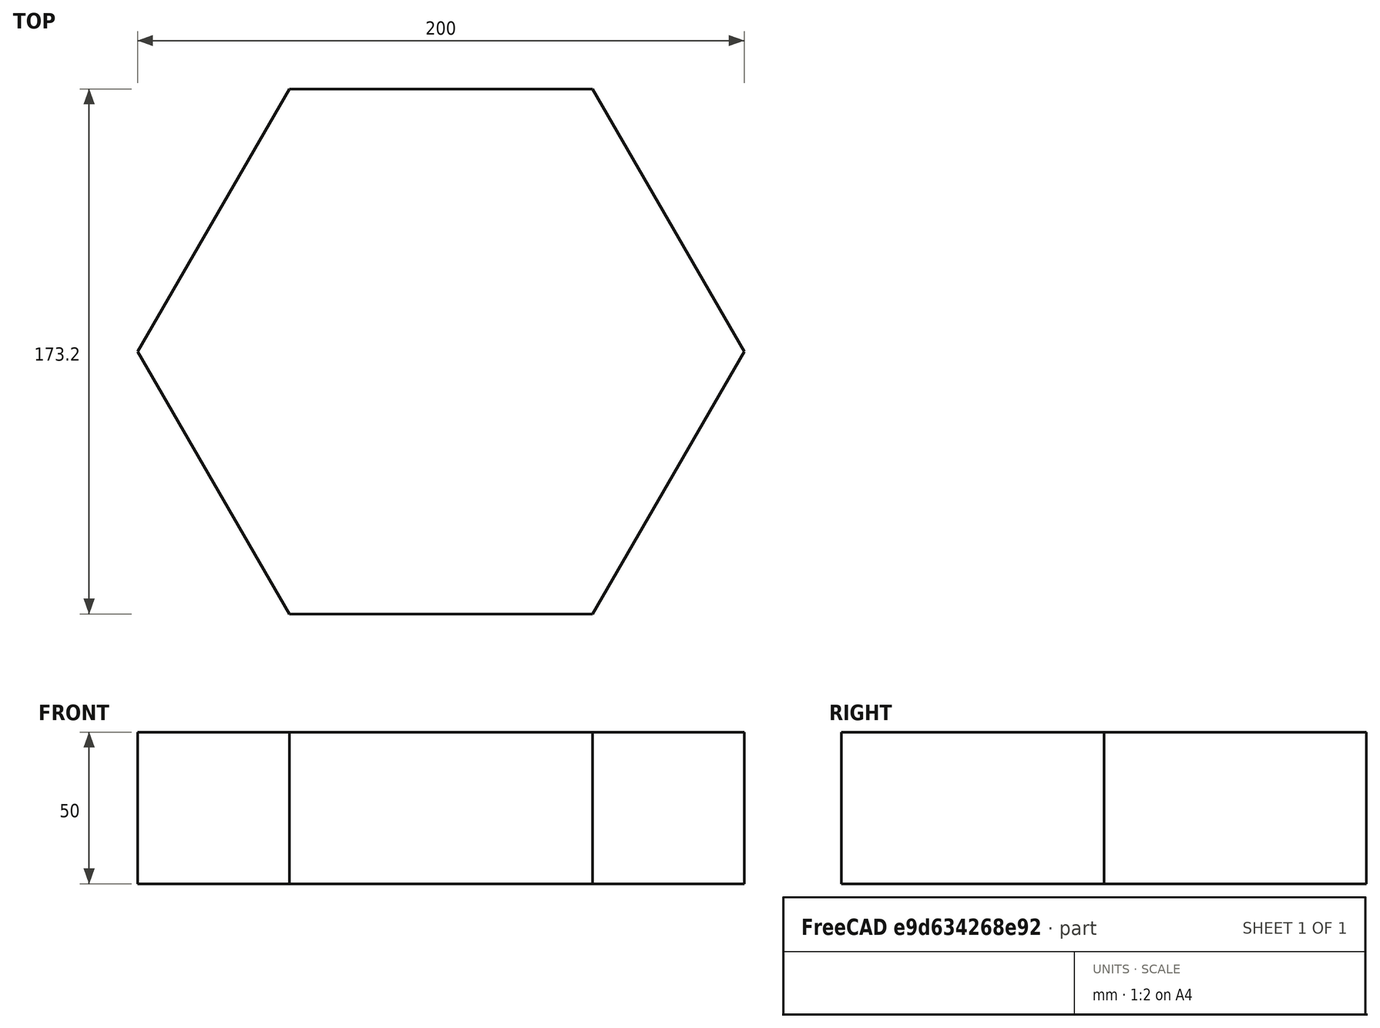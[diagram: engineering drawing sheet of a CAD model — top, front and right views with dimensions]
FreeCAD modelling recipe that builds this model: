
FCSTD DOCUMENT  (FreeCAD 1.0R38806 (Git))
Label: Opgave_2.0.1
License: All rights reserved
LicenseURL: http://en.wikipedia.org/wiki/All_rights_reserved
objects: Sketcher::SketchObject×1, PartDesign::Pad×1, PartDesign::Body×1
note: 6 computed .brp shape members not serialized (recipe doc carries the construction recipe); baked Part::Feature solids carry a one-line shape summary decoded from their .brp

FEATURE [Sketcher::SketchObject] Sketch
  ArcFitTolerance = 1e-06
  AttachmentSupport = -> [XY_Plane]
  FullyConstrained = true
  MakeInternals = false
  MapMode = 5
  sketch-geometry (7):
    g0: LineSegment StartX=100 StartY=0 StartZ=0 EndX=50 EndY=86.6025 EndZ=0
    g1: LineSegment StartX=50 StartY=86.6025 StartZ=0 EndX=-50 EndY=86.6025 EndZ=0
    g2: LineSegment StartX=-50 StartY=86.6025 StartZ=0 EndX=-100 EndY=1.42e-14 EndZ=0
    g3: LineSegment StartX=-100 StartY=1.42e-14 StartZ=0 EndX=-50 EndY=-86.6025 EndZ=0
    g4: LineSegment StartX=-50 StartY=-86.6025 StartZ=0 EndX=50 EndY=-86.6025 EndZ=0
    g5: LineSegment StartX=50 StartY=-86.6025 StartZ=0 EndX=100 EndY=0 EndZ=0
    g6: Circle [constr] CenterX=0 CenterY=0 CenterZ=0 NormalX=0 NormalY=0 NormalZ=1 AngleXU=0 Radius=100
  constraints (16):
    c: Coincident(g0,g1)
    c: Coincident(g1,g2)
    c: Coincident(g2,g3)
    c: Coincident(g3,g4)
    c: Coincident(g4,g5)
    c: Coincident(g5,g0)
    c: Equal(g0, g1-g5) x5
    c: PointOnObject(g0,g6)
    c: PointOnObject(g1,g6)
    c: PointOnObject(g2,g6)
    c: PointOnObject(g3,g6)
    c: PointOnObject(g4,g6)
    c: PointOnObject(g5,g6)
    c: Coincident(g6,g-1)
    c: PointOnObject(g5,g-1)
    c: Diameter(g6) = 200
FEATURE [PartDesign::Pad] Pad
  Direction = (0,0,1)
  Length = 50
  Length2 = 10
  Profile = -> Sketch
  ReferenceAxis = -> Sketch [N_Axis]
  Refine = true
  Suppressed = false
  Type = 0
FEATURE [PartDesign::Body] Body
  AllowCompound = true
  Group = -> [Sketch,Pad]
  Origin = -> Origin
  Tip = -> Pad
